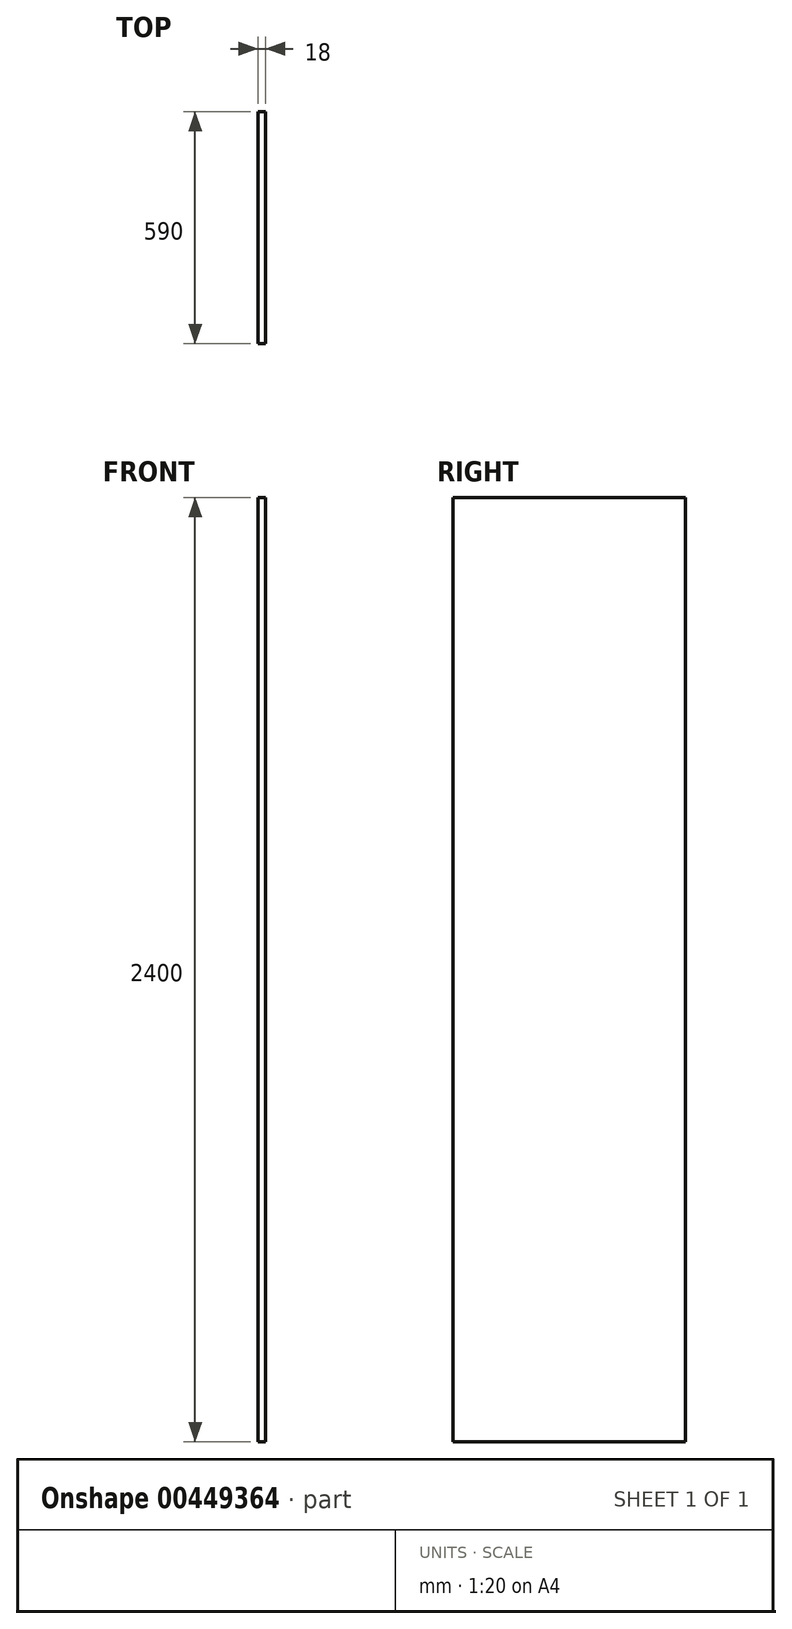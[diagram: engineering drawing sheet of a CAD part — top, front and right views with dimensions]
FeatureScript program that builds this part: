
annotation { "Feature Type Name" : "Feature", "Feature Type Description" : "" }
export const myFeature = defineFeature(function(context is Context, id is Id, definition is map)
    precondition{}
    {
        {
            var Q0;
            Q0=qCreatedBy(makeId("Right.planeOp"),FACE);
            var sketch = newSketch(context, id + "F0", { "sketchPlane" : qUnion([Q0])});
            skLineSegment(sketch, "E0.bottom", {"start": v(0, 2500) * mm, "end": v(590, 2500) * mm});
            skLineSegment(sketch, "E0.top", {"start": v(0, 100) * mm, "end": v(590, 100) * mm});
            skLineSegment(sketch, "E0.left", {"start": v(0, 2500) * mm, "end": v(0, 100) * mm});
            skLineSegment(sketch, "E0.right", {"start": v(590, 2500) * mm, "end": v(590, 100) * mm});
            skSolve(sketch);
        }
        {
            var Q0;
            Q0 = qSketchRegion(id + "F0", true);
            extrude(context, id + "F1", {"entities" : qUnion([Q0]), "oppositeDirection" : true, "depth" : 18 * mm});
        }
    });
